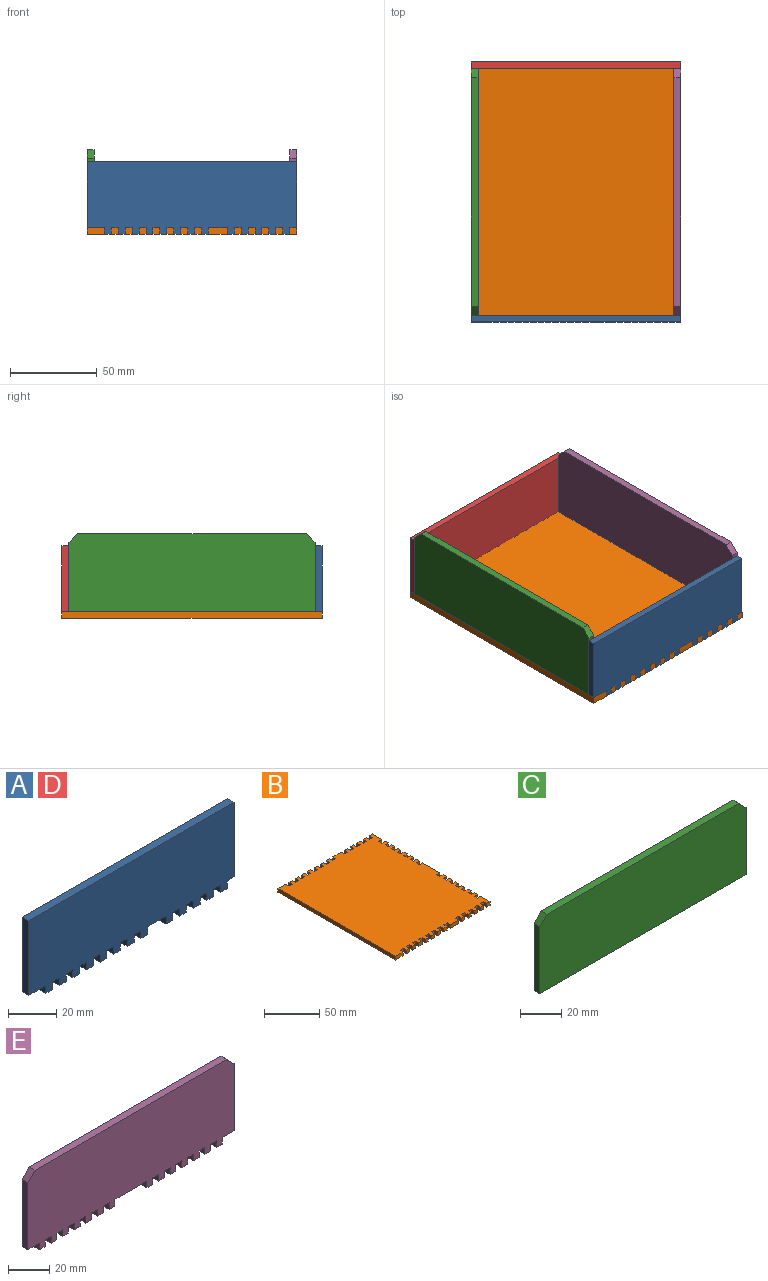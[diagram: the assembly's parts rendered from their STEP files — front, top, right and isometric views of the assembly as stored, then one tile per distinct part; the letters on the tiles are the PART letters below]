
ASSEMBLY  parts=5 mates=4
PART A: 58 faces, bbox 120.9x4x41.9 mm
  f0: plane 4x4mm, normal (1,0,0), area 16mm2, adj f1,f55,f56,f57
  f1: plane 10.87x4mm, normal (0,0,-1), area 43.5mm2, adj f0,f2,f56,f57
  f2: plane 4x4mm, normal (-1,0,0), area 16mm2, adj f1,f3,f56,f57
  f3: plane 4x4mm, normal (0,0,-1), area 16mm2, adj f2,f4,f56,f57
  f4: plane 4x4mm, normal (1,0,0), area 16mm2, adj f3,f5,f56,f57
  f5: plane 4x4mm, normal (0,0,-1), area 16mm2, adj f4,f6,f56,f57
  f6: plane 4x4mm, normal (-1,0,0), area 16mm2, adj f5,f7,f56,f57
  f7: plane 4x4mm, normal (0,0,-1), area 16mm2, adj f6,f8,f56,f57
  f8: plane 4x4mm, normal (1,0,0), area 16mm2, adj f7,f9,f56,f57
  f9: plane 4x4mm, normal (0,0,-1), area 16mm2, adj f8,f10,f56,f57
  f10: plane 4x4mm, normal (-1,0,0), area 16mm2, adj f9,f11,f56,f57
  f11: plane 4x4mm, normal (0,0,-1), area 16mm2, adj f10,f12,f56,f57
  f12: plane 4x4mm, normal (1,0,0), area 16mm2, adj f11,f13,f56,f57
  f13: plane 4x4mm, normal (0,0,-1), area 16mm2, adj f12,f14,f56,f57
  f14: plane 4x4mm, normal (-1,0,0), area 16mm2, adj f13,f15,f56,f57
  f15: plane 4x4mm, normal (0,0,-1), area 16mm2, adj f14,f16,f56,f57
  f16: plane 4x4mm, normal (1,0,0), area 16mm2, adj f15,f17,f56,f57
  f17: plane 4x4mm, normal (0,0,-1), area 16mm2, adj f16,f18,f56,f57
  f18: plane 4x4mm, normal (-1,0,0), area 16mm2, adj f17,f19,f56,f57
  f19: plane 4x4mm, normal (0,0,-1), area 16mm2, adj f18,f20,f56,f57
  f20: plane 4x4mm, normal (1,0,0), area 16mm2, adj f19,f21,f56,f57
  f21: plane 4x4mm, normal (0,0,-1), area 16mm2, adj f20,f22,f56,f57
  f22: plane 37.94x4mm, normal (1,0,0), area 151.8mm2, adj f21,f23,f56,f57
  f23: plane 120.87x4mm, normal (0,0,1), area 483.5mm2, adj f22,f24,f56,f57
  f24: plane 37.94x4mm, normal (-1,0,0), area 151.8mm2, adj f23,f25,f56,f57
  f25: plane 10x4mm, normal (0,0,-1), area 40mm2, adj f24,f26,f56,f57
  f26: plane 4x4mm, normal (-1,0,0), area 16mm2, adj f25,f27,f56,f57
  f27: plane 4x4mm, normal (0,0,-1), area 16mm2, adj f26,f28,f56,f57
  f28: plane 4x4mm, normal (1,0,0), area 16mm2, adj f27,f29,f56,f57
  f29: plane 4x4mm, normal (0,0,-1), area 16mm2, adj f28,f30,f56,f57
  f30: plane 4x4mm, normal (-1,0,0), area 16mm2, adj f29,f31,f56,f57
  f31: plane 4x4mm, normal (0,0,-1), area 16mm2, adj f30,f32,f56,f57
  f32: plane 4x4mm, normal (1,0,0), area 16mm2, adj f31,f33,f56,f57
  f33: plane 4x4mm, normal (0,0,-1), area 16mm2, adj f32,f34,f56,f57
  f34: plane 4x4mm, normal (-1,0,0), area 16mm2, adj f33,f35,f56,f57
  f35: plane 4x4mm, normal (0,0,-1), area 16mm2, adj f34,f36,f56,f57
  f36: plane 4x4mm, normal (1,0,0), area 16mm2, adj f35,f37,f56,f57
  f37: plane 4x4mm, normal (0,0,-1), area 16mm2, adj f36,f38,f56,f57
  f38: plane 4x4mm, normal (-1,0,0), area 16mm2, adj f37,f39,f56,f57
  f39: plane 4x4mm, normal (0,0,-1), area 16mm2, adj f38,f40,f56,f57
  f40: plane 4x4mm, normal (1,0,0), area 16mm2, adj f39,f41,f56,f57
  f41: plane 4x4mm, normal (0,0,-1), area 16mm2, adj f40,f42,f56,f57
  f42: plane 4x4mm, normal (-1,0,0), area 16mm2, adj f41,f43,f56,f57
  f43: plane 4x4mm, normal (0,0,-1), area 16mm2, adj f42,f44,f56,f57
  f44: plane 4x4mm, normal (1,0,0), area 16mm2, adj f43,f45,f56,f57
  f45: plane 4x4mm, normal (0,0,-1), area 16mm2, adj f44,f46,f56,f57
  f46: plane 4x4mm, normal (-1,0,0), area 16mm2, adj f45,f47,f56,f57
  f47: plane 4x4mm, normal (0,0,-1), area 16mm2, adj f46,f48,f56,f57
  f48: plane 4x4mm, normal (1,0,0), area 16mm2, adj f47,f49,f56,f57
  f49: plane 4x4mm, normal (0,0,-1), area 16mm2, adj f48,f50,f56,f57
  f50: plane 4x4mm, normal (-1,0,0), area 16mm2, adj f49,f51,f56,f57
  f51: plane 4x4mm, normal (0,0,-1), area 16mm2, adj f50,f52,f56,f57
  f52: plane 4x4mm, normal (1,0,0), area 16mm2, adj f51,f53,f56,f57
  f53: plane 4x4mm, normal (0,0,-1), area 16mm2, adj f52,f54,f56,f57
  f54: plane 4x4mm, normal (-1,0,0), area 16mm2, adj f53,f55,f56,f57
  f55: plane 4x4mm, normal (0,0,-1), area 16mm2, adj f0,f54,f56,f57
  f56: plane 120.87x41.94mm, normal (0,-1,0), area 4793.8mm2, adj f0,f1,f2,f3,f4,f5,f6,f7
  f57: plane 120.87x41.94mm, normal (0,1,0), area 4793.8mm2, adj f0,f1,f2,f3,f4,f5,f6,f7
PART B: 166 faces, bbox 121x150x4 mm
  f0: plane 4x4mm, normal (0,1,0), area 16mm2, adj f1,f163,f164,f165
  f1: plane 4x4mm, normal (1,0,0), area 16mm2, adj f0,f2,f164,f165
  f2: plane 4x4mm, normal (0,-1,0), area 16mm2, adj f1,f3,f164,f165
  f3: plane 22x4mm, normal (1,-0.01,0), area 88mm2, adj f2,f4,f164,f165
  f4: plane 4.13x4mm, normal (0,1,0), area 16.5mm2, adj f3,f5,f164,f165
  f5: plane 4x4mm, normal (1,0,0), area 16mm2, adj f4,f6,f164,f165
  f6: plane 4.13x4mm, normal (0,-1,0), area 16.5mm2, adj f5,f7,f164,f165
  f7: plane 4x4mm, normal (1,0,0), area 16mm2, adj f6,f8,f164,f165
  f8: plane 4.13x4mm, normal (0,1,0), area 16.5mm2, adj f7,f9,f164,f165
  f9: plane 4x4mm, normal (1,0,0), area 16mm2, adj f8,f10,f164,f165
  f10: plane 4.13x4mm, normal (0,-1,0), area 16.5mm2, adj f9,f11,f164,f165
  f11: plane 4x4mm, normal (1,0,0), area 16mm2, adj f10,f12,f164,f165
  f12: plane 4.13x4mm, normal (0,1,0), area 16.5mm2, adj f11,f13,f164,f165
  f13: plane 4x4mm, normal (1,0,0), area 16mm2, adj f12,f14,f164,f165
  f14: plane 4.13x4mm, normal (0,-1,0), area 16.5mm2, adj f13,f15,f164,f165
  f15: plane 4x4mm, normal (1,0,0), area 16mm2, adj f14,f16,f164,f165
  f16: plane 4.13x4mm, normal (0,1,0), area 16.5mm2, adj f15,f17,f164,f165
  f17: plane 4x4mm, normal (1,0,0), area 16mm2, adj f16,f18,f164,f165
  f18: plane 4.13x4mm, normal (0,-1,0), area 16.5mm2, adj f17,f19,f164,f165
  f19: plane 4x4mm, normal (1,0,0), area 16mm2, adj f18,f20,f164,f165
  f20: plane 4.13x4mm, normal (0,1,0), area 16.5mm2, adj f19,f21,f164,f165
  f21: plane 4x4mm, normal (1,0,0), area 16mm2, adj f20,f22,f164,f165
  f22: plane 4.13x4mm, normal (0,-1,0), area 16.5mm2, adj f21,f23,f164,f165
  f23: plane 4x4mm, normal (1,0,0), area 16mm2, adj f22,f24,f164,f165
  f24: plane 4.13x4mm, normal (0,1,0), area 16.5mm2, adj f23,f25,f164,f165
  f25: plane 4x4mm, normal (1,0,0), area 16mm2, adj f24,f26,f164,f165
  f26: plane 4.13x4mm, normal (0,-1,0), area 16.5mm2, adj f25,f27,f164,f165
  f27: plane 4x4mm, normal (1,0,0), area 16mm2, adj f26,f28,f164,f165
  f28: plane 4.13x4mm, normal (0,1,0), area 16.5mm2, adj f27,f29,f164,f165
  f29: plane 4x4mm, normal (1,0,0), area 16mm2, adj f28,f30,f164,f165
  f30: plane 4x4mm, normal (0,-1,0), area 16mm2, adj f29,f31,f164,f165
  f31: plane 12x4mm, normal (1,0,0), area 48mm2, adj f30,f32,f164,f165
  f32: plane 4x4mm, normal (0,1,0), area 16mm2, adj f31,f33,f164,f165
  f33: plane 4x4mm, normal (-1,0,0), area 16mm2, adj f32,f34,f164,f165
  f34: plane 4x4mm, normal (0,1,0), area 16mm2, adj f33,f35,f164,f165
  f35: plane 4x4mm, normal (1,0,0), area 16mm2, adj f34,f36,f164,f165
  f36: plane 4x4mm, normal (0,1,0), area 16mm2, adj f35,f37,f164,f165
  f37: plane 4x4mm, normal (-1,0,0), area 16mm2, adj f36,f38,f164,f165
  f38: plane 4x4mm, normal (0,1,0), area 16mm2, adj f37,f39,f164,f165
  f39: plane 4x4mm, normal (1,0,0), area 16mm2, adj f38,f40,f164,f165
  f40: plane 4x4mm, normal (0,1,0), area 16mm2, adj f39,f41,f164,f165
  f41: plane 4x4mm, normal (-1,0,0), area 16mm2, adj f40,f42,f164,f165
  f42: plane 4x4mm, normal (0,1,0), area 16mm2, adj f41,f43,f164,f165
  f43: plane 4x4mm, normal (1,0,0), area 16mm2, adj f42,f44,f164,f165
  f44: plane 4x4mm, normal (0,1,0), area 16mm2, adj f43,f45,f164,f165
  f45: plane 4x4mm, normal (-1,0,0), area 16mm2, adj f44,f46,f164,f165
  f46: plane 4x4mm, normal (0,1,0), area 16mm2, adj f45,f47,f164,f165
  f47: plane 4x4mm, normal (1,0,0), area 16mm2, adj f46,f48,f164,f165
  f48: plane 4x4mm, normal (0,1,0), area 16mm2, adj f47,f49,f164,f165
  f49: plane 4x4mm, normal (-1,0,0), area 16mm2, adj f48,f50,f164,f165
  f50: plane 4x4mm, normal (0,1,0), area 16mm2, adj f49,f51,f164,f165
  f51: plane 4x4mm, normal (1,0,0), area 16mm2, adj f50,f52,f164,f165
  f52: plane 10.87x4mm, normal (0,1,0), area 43.5mm2, adj f51,f53,f164,f165
  f53: plane 4x4mm, normal (-1,0,0), area 16mm2, adj f52,f54,f164,f165
  f54: plane 4x4mm, normal (0,1,0), area 16mm2, adj f53,f55,f164,f165
  f55: plane 4x4mm, normal (1,0,0), area 16mm2, adj f54,f56,f164,f165
  f56: plane 4x4mm, normal (0,1,0), area 16mm2, adj f55,f57,f164,f165
  f57: plane 4x4mm, normal (-1,0,0), area 16mm2, adj f56,f58,f164,f165
  f58: plane 4x4mm, normal (0,1,0), area 16mm2, adj f57,f59,f164,f165
  f59: plane 4x4mm, normal (1,0,0), area 16mm2, adj f58,f60,f164,f165
  f60: plane 4x4mm, normal (0,1,0), area 16mm2, adj f59,f61,f164,f165
  f61: plane 4x4mm, normal (-1,0,0), area 16mm2, adj f60,f62,f164,f165
  f62: plane 4x4mm, normal (0,1,0), area 16mm2, adj f61,f63,f164,f165
  f63: plane 4x4mm, normal (1,0,0), area 16mm2, adj f62,f64,f164,f165
  f64: plane 4x4mm, normal (0,1,0), area 16mm2, adj f63,f65,f164,f165
  f65: plane 4x4mm, normal (-1,0,0), area 16mm2, adj f64,f66,f164,f165
  f66: plane 4x4mm, normal (0,1,0), area 16mm2, adj f65,f67,f164,f165
  f67: plane 4x4mm, normal (1,0,0), area 16mm2, adj f66,f68,f164,f165
  f68: plane 4x4mm, normal (0,1,0), area 16mm2, adj f67,f69,f164,f165
  f69: plane 4x4mm, normal (-1,0,0), area 16mm2, adj f68,f70,f164,f165
  f70: plane 4x4mm, normal (0,1,0), area 16mm2, adj f69,f71,f164,f165
  f71: plane 4x4mm, normal (1,0,0), area 16mm2, adj f70,f72,f164,f165
  f72: plane 4x4mm, normal (0,1,0), area 16mm2, adj f71,f73,f164,f165
  f73: plane 4x4mm, normal (-1,0,0), area 16mm2, adj f72,f74,f164,f165
  f74: plane 4x4mm, normal (0,1,0), area 16mm2, adj f73,f75,f164,f165
  f75: plane 4x4mm, normal (1,0,0), area 16mm2, adj f74,f76,f164,f165
  f76: plane 4x4mm, normal (0,1,0), area 16mm2, adj f75,f77,f164,f165
  f77: plane 4x4mm, normal (-1,0,0), area 16mm2, adj f76,f78,f164,f165
  f78: plane 4x4mm, normal (0,1,0), area 16mm2, adj f77,f79,f164,f165
  f79: plane 4x4mm, normal (1,0,0), area 16mm2, adj f78,f80,f164,f165
  f80: plane 4x4mm, normal (0,1,0), area 16mm2, adj f79,f81,f164,f165
  f81: plane 4x4mm, normal (-1,0,0), area 16mm2, adj f80,f82,f164,f165
  f82: plane 4x4mm, normal (0,1,0), area 16mm2, adj f81,f83,f164,f165
  f83: plane 4x4mm, normal (1,0,0), area 16mm2, adj f82,f84,f164,f165
  f84: plane 10x4mm, normal (0,1,0), area 40mm2, adj f83,f85,f164,f165
  f85: plane 150x4mm, normal (-1,0,0), area 600mm2, adj f84,f86,f164,f165
  f86: plane 10x4mm, normal (0,-1,0), area 40mm2, adj f85,f87,f164,f165
  f87: plane 4x4mm, normal (1,0,0), area 16mm2, adj f86,f88,f164,f165
  f88: plane 4x4mm, normal (0,-1,0), area 16mm2, adj f87,f89,f164,f165
  f89: plane 4x4mm, normal (-1,0,0), area 16mm2, adj f88,f90,f164,f165
  f90: plane 4x4mm, normal (0,-1,0), area 16mm2, adj f89,f91,f164,f165
  f91: plane 4x4mm, normal (1,0,0), area 16mm2, adj f90,f92,f164,f165
  f92: plane 4x4mm, normal (0,-1,0), area 16mm2, adj f91,f93,f164,f165
  f93: plane 4x4mm, normal (-1,0,0), area 16mm2, adj f92,f94,f164,f165
  f94: plane 4x4mm, normal (0,-1,0), area 16mm2, adj f93,f95,f164,f165
  f95: plane 4x4mm, normal (1,0,0), area 16mm2, adj f94,f96,f164,f165
  f96: plane 4x4mm, normal (0,-1,0), area 16mm2, adj f95,f97,f164,f165
  f97: plane 4x4mm, normal (-1,0,0), area 16mm2, adj f96,f98,f164,f165
  f98: plane 4x4mm, normal (0,-1,0), area 16mm2, adj f97,f99,f164,f165
  f99: plane 4x4mm, normal (1,0,0), area 16mm2, adj f98,f100,f164,f165
  f100: plane 4x4mm, normal (0,-1,0), area 16mm2, adj f99,f101,f164,f165
  f101: plane 4x4mm, normal (-1,0,0), area 16mm2, adj f100,f102,f164,f165
  f102: plane 4x4mm, normal (0,-1,0), area 16mm2, adj f101,f103,f164,f165
  f103: plane 4x4mm, normal (1,0,0), area 16mm2, adj f102,f104,f164,f165
  f104: plane 4x4mm, normal (0,-1,0), area 16mm2, adj f103,f105,f164,f165
  f105: plane 4x4mm, normal (-1,0,0), area 16mm2, adj f104,f106,f164,f165
  f106: plane 4x4mm, normal (0,-1,0), area 16mm2, adj f105,f107,f164,f165
  f107: plane 4x4mm, normal (1,0,0), area 16mm2, adj f106,f108,f164,f165
  f108: plane 4x4mm, normal (0,-1,0), area 16mm2, adj f107,f109,f164,f165
  f109: plane 4x4mm, normal (-1,0,0), area 16mm2, adj f108,f110,f164,f165
  f110: plane 4x4mm, normal (0,-1,0), area 16mm2, adj f109,f111,f164,f165
  f111: plane 4x4mm, normal (1,0,0), area 16mm2, adj f110,f112,f164,f165
  f112: plane 4x4mm, normal (0,-1,0), area 16mm2, adj f111,f113,f164,f165
  f113: plane 4x4mm, normal (-1,0,0), area 16mm2, adj f112,f114,f164,f165
  f114: plane 4x4mm, normal (0,-1,0), area 16mm2, adj f113,f115,f164,f165
  f115: plane 4x4mm, normal (1,0,0), area 16mm2, adj f114,f116,f164,f165
  f116: plane 4x4mm, normal (0,-1,0), area 16mm2, adj f115,f117,f164,f165
  f117: plane 4x4mm, normal (-1,0,0), area 16mm2, adj f116,f118,f164,f165
  f118: plane 10.87x4mm, normal (0,-1,0), area 43.5mm2, adj f117,f119,f164,f165
  f119: plane 4x4mm, normal (1,0,0), area 16mm2, adj f118,f120,f164,f165
  f120: plane 4x4mm, normal (0,-1,0), area 16mm2, adj f119,f121,f164,f165
  f121: plane 4x4mm, normal (-1,0,0), area 16mm2, adj f120,f122,f164,f165
  f122: plane 4x4mm, normal (0,-1,0), area 16mm2, adj f121,f123,f164,f165
  f123: plane 4x4mm, normal (1,0,0), area 16mm2, adj f122,f124,f164,f165
  f124: plane 4x4mm, normal (0,-1,0), area 16mm2, adj f123,f125,f164,f165
  f125: plane 4x4mm, normal (-1,0,0), area 16mm2, adj f124,f126,f164,f165
  f126: plane 4x4mm, normal (0,-1,0), area 16mm2, adj f125,f127,f164,f165
  f127: plane 4x4mm, normal (1,0,0), area 16mm2, adj f126,f128,f164,f165
  f128: plane 4x4mm, normal (0,-1,0), area 16mm2, adj f127,f129,f164,f165
  f129: plane 4x4mm, normal (-1,0,0), area 16mm2, adj f128,f130,f164,f165
  f130: plane 4x4mm, normal (0,-1,0), area 16mm2, adj f129,f131,f164,f165
  f131: plane 4x4mm, normal (1,0,0), area 16mm2, adj f130,f132,f164,f165
  f132: plane 4x4mm, normal (0,-1,0), area 16mm2, adj f131,f133,f164,f165
  f133: plane 4x4mm, normal (-1,0,0), area 16mm2, adj f132,f134,f164,f165
  f134: plane 4x4mm, normal (0,-1,0), area 16mm2, adj f133,f135,f164,f165
  f135: plane 4x4mm, normal (1,0,0), area 16mm2, adj f134,f136,f164,f165
  f136: plane 4x4mm, normal (0,-1,0), area 16mm2, adj f135,f137,f164,f165
  f137: plane 4x4mm, normal (-1,0,0), area 16mm2, adj f136,f138,f164,f165
  f138: plane 4x4mm, normal (0,-1,0), area 16mm2, adj f137,f139,f164,f165
  f139: plane 12x4mm, normal (1,0,0), area 48mm2, adj f138,f140,f164,f165
  f140: plane 4x4mm, normal (0,1,0), area 16mm2, adj f139,f141,f164,f165
  f141: plane 4x4mm, normal (1,0,0), area 16mm2, adj f140,f142,f164,f165
  f142: plane 4x4mm, normal (0,-1,0), area 16mm2, adj f141,f143,f164,f165
  f143: plane 4x4mm, normal (1,0,0), area 16mm2, adj f142,f144,f164,f165
  f144: plane 4x4mm, normal (0,1,0), area 16mm2, adj f143,f145,f164,f165
  f145: plane 4x4mm, normal (1,0,0), area 16mm2, adj f144,f146,f164,f165
  f146: plane 4x4mm, normal (0,-1,0), area 16mm2, adj f145,f147,f164,f165
  f147: plane 4x4mm, normal (1,0,0), area 16mm2, adj f146,f148,f164,f165
  f148: plane 4x4mm, normal (0,1,0), area 16mm2, adj f147,f149,f164,f165
  f149: plane 4x4mm, normal (1,0,0), area 16mm2, adj f148,f150,f164,f165
  f150: plane 4x4mm, normal (0,-1,0), area 16mm2, adj f149,f151,f164,f165
  f151: plane 4x4mm, normal (1,0,0), area 16mm2, adj f150,f152,f164,f165
  f152: plane 4x4mm, normal (0,1,0), area 16mm2, adj f151,f153,f164,f165
  f153: plane 4x4mm, normal (1,0,0), area 16mm2, adj f152,f154,f164,f165
  f154: plane 4x4mm, normal (0,-1,0), area 16mm2, adj f153,f155,f164,f165
  f155: plane 4x4mm, normal (1,0,0), area 16mm2, adj f154,f156,f164,f165
  f156: plane 4x4mm, normal (0,1,0), area 16mm2, adj f155,f157,f164,f165
  f157: plane 4x4mm, normal (1,0,0), area 16mm2, adj f156,f158,f164,f165
  f158: plane 4x4mm, normal (0,-1,0), area 16mm2, adj f157,f159,f164,f165
  f159: plane 4x4mm, normal (1,0,0), area 16mm2, adj f158,f160,f164,f165
  f160: plane 4x4mm, normal (0,1,0), area 16mm2, adj f159,f161,f164,f165
  f161: plane 4x4mm, normal (1,0,0), area 16mm2, adj f160,f162,f164,f165
  f162: plane 4x4mm, normal (0,-1,0), area 16mm2, adj f161,f163,f164,f165
  f163: plane 4x4mm, normal (1,0,0), area 16mm2, adj f0,f162,f164,f165
  f164: plane 150x121mm, normal (0,0,1), area 17495.1mm2, adj f0,f1,f2,f3,f4,f5,f6,f7
  f165: plane 150x121mm, normal (0,0,-1), area 17495.1mm2, adj f0,f1,f2,f3,f4,f5,f6,f7
PART C: 8 faces, bbox 142x4x45 mm
  f0: plane 40x4mm, normal (1,0,0), area 160mm2, adj f3,f4,f5,f7
  f1: plane 132x4mm, normal (0,0,1), area 528mm2, adj f4,f5,f6,f7
  f2: plane 40x4mm, normal (-1,0,0), area 160mm2, adj f3,f4,f5,f6
  f3: plane 142x4mm, normal (0,0,-1), area 568mm2, adj f0,f2,f4,f5
  f4: plane 142x45mm, normal (0,-1,0), area 6365mm2, adj f0,f1,f2,f3,f6,f7
  f5: plane 142x45mm, normal (0,1,0), area 6365mm2, adj f0,f1,f2,f3,f6,f7
  f6: plane 5x5mm, normal (-0.71,0,0.71), area 28.3mm2, adj f1,f2,f4,f5
  f7: plane 5x5mm, normal (0.71,0,0.71), area 28.3mm2, adj f0,f1,f4,f5
PART D: same geometry as A
PART E: 64 faces, bbox 142x4x49 mm
  f0: plane 132x4mm, normal (0,0,1), area 528mm2, adj f60,f61,f62,f63
  f1: plane 40x4mm, normal (-1,0,0), area 160mm2, adj f2,f60,f61,f63
  f2: plane 8x4mm, normal (0,0,-1), area 32mm2, adj f1,f3,f60,f61
  f3: plane 4x4mm, normal (-1,0,0), area 16mm2, adj f2,f4,f60,f61
  f4: plane 4x4mm, normal (0,0,-1), area 16mm2, adj f3,f5,f60,f61
  f5: plane 4x4mm, normal (1,0,0), area 16mm2, adj f4,f6,f60,f61
  f6: plane 4x4mm, normal (0,0,-1), area 16mm2, adj f5,f7,f60,f61
  f7: plane 4x4mm, normal (-1,0,0), area 16mm2, adj f6,f8,f60,f61
  f8: plane 4x4mm, normal (0,0,-1), area 16mm2, adj f7,f9,f60,f61
  f9: plane 4x4mm, normal (1,0,0), area 16mm2, adj f8,f10,f60,f61
  f10: plane 4x4mm, normal (0,0,-1), area 16mm2, adj f9,f11,f60,f61
  f11: plane 4x4mm, normal (-1,0,0), area 16mm2, adj f10,f12,f60,f61
  f12: plane 4x4mm, normal (0,0,-1), area 16mm2, adj f11,f13,f60,f61
  f13: plane 4x4mm, normal (1,0,0), area 16mm2, adj f12,f14,f60,f61
  f14: plane 4x4mm, normal (0,0,-1), area 16mm2, adj f13,f15,f60,f61
  f15: plane 4x4mm, normal (-1,0,0), area 16mm2, adj f14,f16,f60,f61
  f16: plane 4x4mm, normal (0,0,-1), area 16mm2, adj f15,f17,f60,f61
  f17: plane 4x4mm, normal (1,0,0), area 16mm2, adj f16,f18,f60,f61
  f18: plane 4x4mm, normal (0,0,-1), area 16mm2, adj f17,f19,f60,f61
  f19: plane 4x4mm, normal (-1,0,0), area 16mm2, adj f18,f20,f60,f61
  f20: plane 4x4mm, normal (0,0,-1), area 16mm2, adj f19,f21,f60,f61
  f21: plane 4x4mm, normal (1,0,0), area 16mm2, adj f20,f22,f60,f61
  f22: plane 4x4mm, normal (0,0,-1), area 16mm2, adj f21,f23,f60,f61
  f23: plane 4x4mm, normal (-1,0,0), area 16mm2, adj f22,f24,f60,f61
  f24: plane 4x4mm, normal (0,0,-1), area 16mm2, adj f23,f25,f60,f61
  f25: plane 4x4mm, normal (1,0,0), area 16mm2, adj f24,f26,f60,f61
  f26: plane 4x4mm, normal (0,0,-1), area 16mm2, adj f25,f27,f60,f61
  f27: plane 4x4mm, normal (-1,0,0), area 16mm2, adj f26,f28,f60,f61
  f28: plane 4x4mm, normal (0,0,-1), area 16mm2, adj f27,f29,f60,f61
  f29: plane 4x4mm, normal (1,0,0), area 16mm2, adj f28,f30,f60,f61
  f30: plane 22x4mm, normal (0,0,-1), area 88mm2, adj f29,f31,f60,f61
  f31: plane 4x4mm, normal (-1,0,0), area 16mm2, adj f30,f32,f60,f61
  f32: plane 4x4mm, normal (0,0,-1), area 16mm2, adj f31,f33,f60,f61
  f33: plane 4x4mm, normal (1,0,0), area 16mm2, adj f32,f34,f60,f61
  f34: plane 4x4mm, normal (0,0,-1), area 16mm2, adj f33,f35,f60,f61
  f35: plane 4x4mm, normal (-1,0,0), area 16mm2, adj f34,f36,f60,f61
  f36: plane 4x4mm, normal (0,0,-1), area 16mm2, adj f35,f37,f60,f61
  f37: plane 4x4mm, normal (1,0,0), area 16mm2, adj f36,f38,f60,f61
  f38: plane 4x4mm, normal (0,0,-1), area 16mm2, adj f37,f39,f60,f61
  f39: plane 4x4mm, normal (-1,0,0), area 16mm2, adj f38,f40,f60,f61
  f40: plane 4x4mm, normal (0,0,-1), area 16mm2, adj f39,f41,f60,f61
  f41: plane 4x4mm, normal (1,0,0), area 16mm2, adj f40,f42,f60,f61
  f42: plane 4x4mm, normal (0,0,-1), area 16mm2, adj f41,f43,f60,f61
  f43: plane 4x4mm, normal (-1,0,0), area 16mm2, adj f42,f44,f60,f61
  f44: plane 4x4mm, normal (0,0,-1), area 16mm2, adj f43,f45,f60,f61
  f45: plane 4x4mm, normal (1,0,0), area 16mm2, adj f44,f46,f60,f61
  f46: plane 4x4mm, normal (0,0,-1), area 16mm2, adj f45,f47,f60,f61
  f47: plane 4x4mm, normal (-1,0,0), area 16mm2, adj f46,f48,f60,f61
  f48: plane 4x4mm, normal (0,0,-1), area 16mm2, adj f47,f49,f60,f61
  f49: plane 4x4mm, normal (1,0,0), area 16mm2, adj f48,f50,f60,f61
  f50: plane 4x4mm, normal (0,0,-1), area 16mm2, adj f49,f51,f60,f61
  f51: plane 4x4mm, normal (-1,0,0), area 16mm2, adj f50,f52,f60,f61
  f52: plane 4x4mm, normal (0,0,-1), area 16mm2, adj f51,f53,f60,f61
  f53: plane 4x4mm, normal (1,0,0), area 16mm2, adj f52,f54,f60,f61
  f54: plane 4x4mm, normal (0,0,-1), area 16mm2, adj f53,f55,f60,f61
  f55: plane 4x4mm, normal (-1,0,0), area 16mm2, adj f54,f56,f60,f61
  f56: plane 4x4mm, normal (0,0,-1), area 16mm2, adj f55,f57,f60,f61
  f57: plane 4x4mm, normal (1,0,0), area 16mm2, adj f56,f58,f60,f61
  f58: plane 8x4mm, normal (0,0,-1), area 32mm2, adj f57,f59,f60,f61
  f59: plane 40x4mm, normal (1,0,0), area 160mm2, adj f58,f60,f61,f62
  f60: plane 142x49mm, normal (0,-1,0), area 6589mm2, adj f0,f1,f2,f3,f4,f5,f6,f7
  f61: plane 142x49mm, normal (0,1,0), area 6589mm2, adj f0,f1,f2,f3,f4,f5,f6,f7
  f62: plane 5x5mm, normal (0.71,0,0.71), area 28.3mm2, adj f0,f59,f60,f61
  f63: plane 5x5mm, normal (-0.71,0,0.71), area 28.3mm2, adj f0,f1,f60,f61
PLACE A t=(86.65,-43.35,-1.67)mm
PLACE B t=(86.69,-42.58,-20.64)mm
PLACE C rot(axis=(0,0,1),90deg) t=(11.21,27.65,3.86)mm
PLACE D t=(86.65,102.65,-1.67)mm
PLACE E rot(axis=(0,0,1),90deg) t=(130.15,27.65,-1.89)mm
MATE fastened C.f3 <-> B.f164  axis (0,0,-1) through (11.21,27.65,-18.64)mm
MATE fastened D.f1 <-> B.f164  axis (0,0,-1) through (86.65,102.65,-18.64)mm
MATE fastened E.f30 <-> B.f164  axis (0,0,-1) through (132.15,27.65,-18.64)mm
MATE fastened A.f1 <-> B.f164  axis (0,0,-1) through (86.65,-47.35,-18.64)mm
